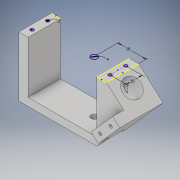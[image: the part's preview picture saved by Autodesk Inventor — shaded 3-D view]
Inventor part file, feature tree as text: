
AUTODESK INVENTOR PART (.ipt)
format: ipt  version: 2019 (Build 230136000, 136)  size: 181,248 bytes
history: native  units: mm
features: extrude x6, sketch x5, other x1
ambient origin geometry x8: Origin, YZ Plane, XZ Plane, XY Plane, X Axis, Y Axis, Z Axis, Center Point
bodies: Body1 (feature_tree)
feature tree (12):
  other  "Твердое тело1"
  extrude  "Выдавливание1"  Depth=5.0mm
  extrude  "Выдавливание2"  Depth=6.0mm
  sketch  "Эскиз3"
  extrude  "Выдавливание3"  Depth=43.5mm
  extrude  "Выдавливание4"  Depth=6.0mm
  extrude  "Выдавливание5"  Depth=38.0mm
  extrude  "Выдавливание6"  Depth=38.0mm
  sketch  "Эскиз1"
  sketch  "Эскиз2"
  sketch  "Эскиз4"
  sketch  "Эскиз5"
